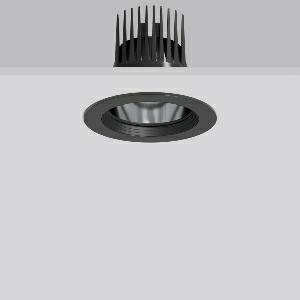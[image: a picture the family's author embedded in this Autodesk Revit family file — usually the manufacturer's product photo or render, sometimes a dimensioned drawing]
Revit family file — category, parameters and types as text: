
# Revit family: heledon_maxi_e_901771_003_76_da20
name_source: partatom
category: Lighting Fixtures
units: mm (PartAtom-declared; Revit-internal decimal feet)

## family parameters
Cut with Voids When Loaded = No
Host = Face
Light Source = No
Part Type = Normal
Room Calculation Point = No
Round Connector Dimension = Use Diameter
Shared = No

## types (1)
- HELEDON maxi E (1 x LED Modul 932 fresh meat, 2150 lm, 3200)
    Apparent Load = 33 VA
    Approval mark = CE
    CIE Flux Codes = 100 100 100 100 100
    Color Rendering = 90
    Color Temperature = 3200
    Default Elevation = 1800 mm
    Description = Series: HELEDON maxi
Round recessed downlight. Housing: die-cast aluminium, powder-coated. Black plastic ring and recessed LED to prevent glare from the side. Optical assembly with reflector made of MIRO-Silver with 98% total light reflection for outstanding efficiency - can be changed without tools. Special LED for illumination of meat included. Suitable for Recessed ceiling mounting. Installation without tools thanks to spring fastening system. Including separate LED converter with connecting cable 600 mm.High quality converter without flickering and stroboscopic effect. Through-wiring box (5 pole) available as accessory. The following accessories can be mounted without use of tools: interchangeable lenses, decorative glasses, honeycomb louvre, clear and frosted diffusers, white interchangeable plastic ring. 
Colour: deep black, matt (RAL 9005)
Diameter: 162 mm
Height: 3 mm
Cut-out diameter: 152 mm
Recess height: 200 mm
Luminaire: recess height: 135 mm
Lamp: LED
Socket: without socket
Colour temperature: fresh meat
System power: 33 W
Rated luminous flux: 2150 lm
Luminous efficiency: 65 lm/W
Control gear: Converter, dimmable, DALI
Protection class: II
Type of protection: IP 20
    Height = 0 mm  [stored 0 ft]
    Lamp = 1 x LED Modul 932 fresh meat
    Lamp Light Flux = 2150 lm
    Lamp count = 1
    Length = 162 mm
    Lifetime = 50000 h
    Luminous efficacy = 65 lm/W
    Manufacturer = RZB
    ModVariant = No
    Model = 901771.003.76
    Mounting Place = Ceiling
    Mounting Type = Recessed
    Number of Poles = 1
    OnlyDefault = Yes
    Power Factor = 1
    Product Name = HELEDON maxi E
    Product group = Recessed downlights
    ProductGroupID = 402
    Protection Class = Protection class II
    Protection Degree = IP 20
    RLX_Detail_Level = 1
    RLX_Emergency_Light_Flux = 0 lm
    RLX_Emergency_Type = 0
    RLX_Emergency_Type_DB = No
    RlxData = <blob elided: 121157 chars, md5=7814c524>
    Socket = socket
    Standby Power = 0 W
    System Light Flux = 2150 lm
    System Power = 33 W
    Type Comments = Product without accessories
    Type Image = 901662.003.jpg
    URL = http://relux.com
    VarID = ---
    Voltage = 230 V
    Voltage Range = 220-240 V
    Weight = 0.00 kg
    Width = 0 mm  [stored 0 ft]

note: [stored X ft] marks values corroborated as IEEE doubles in the binary element streams (Revit-internal decimal feet)

## geometry (parser evidence)
native form markers: Blend x4, Sweep x12
no freeform markers — native parametric forms only
